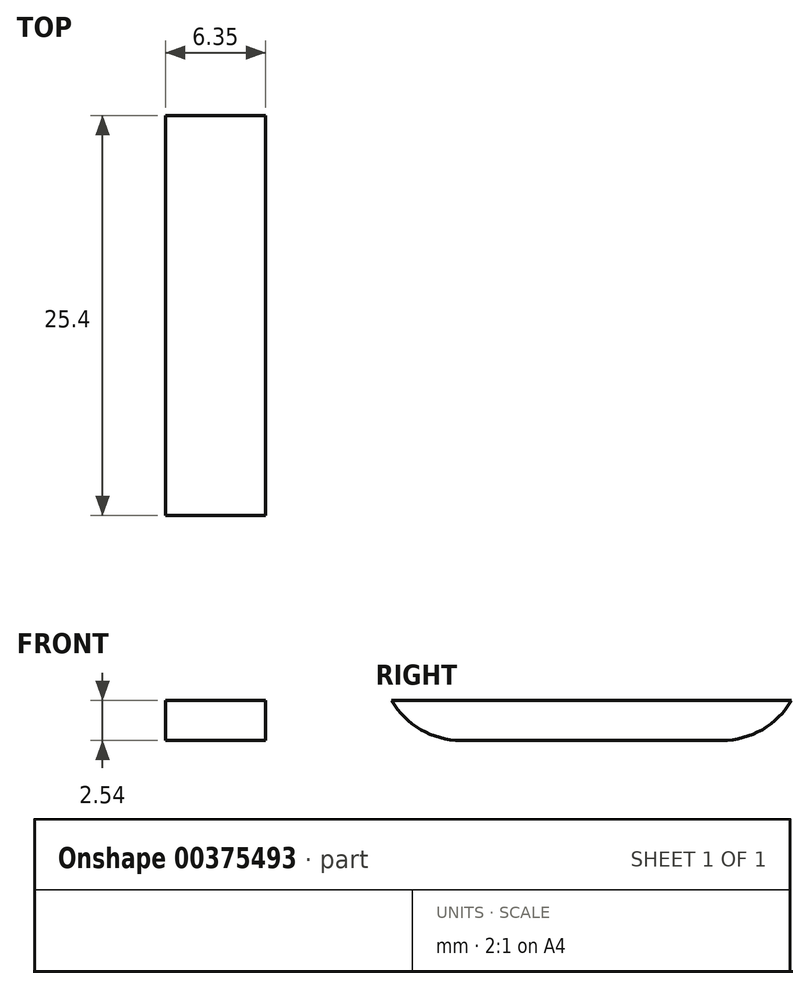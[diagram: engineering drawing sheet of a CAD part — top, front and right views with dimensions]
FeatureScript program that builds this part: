
annotation { "Feature Type Name" : "Feature", "Feature Type Description" : "" }
export const myFeature = defineFeature(function(context is Context, id is Id, definition is map)
    precondition{}
    {
        {
            var Q0;
            Q0=qCreatedBy(makeId("Top.planeOp"),FACE);
            var sketch = newSketch(context, id + "F0", { "sketchPlane" : qUnion([Q0])});
            skLineSegment(sketch, "E0", {"start": v(-10.91, 34.11) * mm, "end": v(-10.91, 8.71) * mm});
            skLineSegment(sketch, "E1", {"start": v(-10.91, 8.71) * mm, "end": v(-4.56, 8.71) * mm});
            skLineSegment(sketch, "E2", {"start": v(-4.56, 8.71) * mm, "end": v(-4.56, 34.11) * mm});
            skLineSegment(sketch, "E3", {"start": v(-4.56, 34.11) * mm, "end": v(-10.91, 34.11) * mm});
            skSolve(sketch);
        }
        {
            var Q0;
            Q0=makeQuery(id+"F0.imprint","IMPRINT",FACE,{"disambiguationData":[TD([[makeQuery(id+"F0.imprint","IMPRINT",EDGE,{"derivedFrom":sQuery(id+"F0.wireOp",EDGE,"E0")}),1.0]])]});
            extrude(context, id + "F1", {"entities" : qUnion([Q0]), "depth" : 2.54 * mm});
        }
        {
            var Q0;
            Q0=makeQuery(id+"F1.opExtrude","CAP_EDGE",EDGE,{"disambiguationData":[OSD([sQuery(id+"F0.wireOp",EDGE,"E1")])],"isStart":true});
            var Q1;
            Q1=makeQuery(id+"F1.opExtrude","CAP_EDGE",EDGE,{"disambiguationData":[OSD([sQuery(id+"F0.wireOp",EDGE,"E3")])],"isStart":true});
            fillet(context, id + "F2", {"entities" : qUnion([Q0, Q1]), "radius" : 5.08 * mm, "tangentPropagation" : true, "allowEdgeOverflow" : false});
        }
    });
